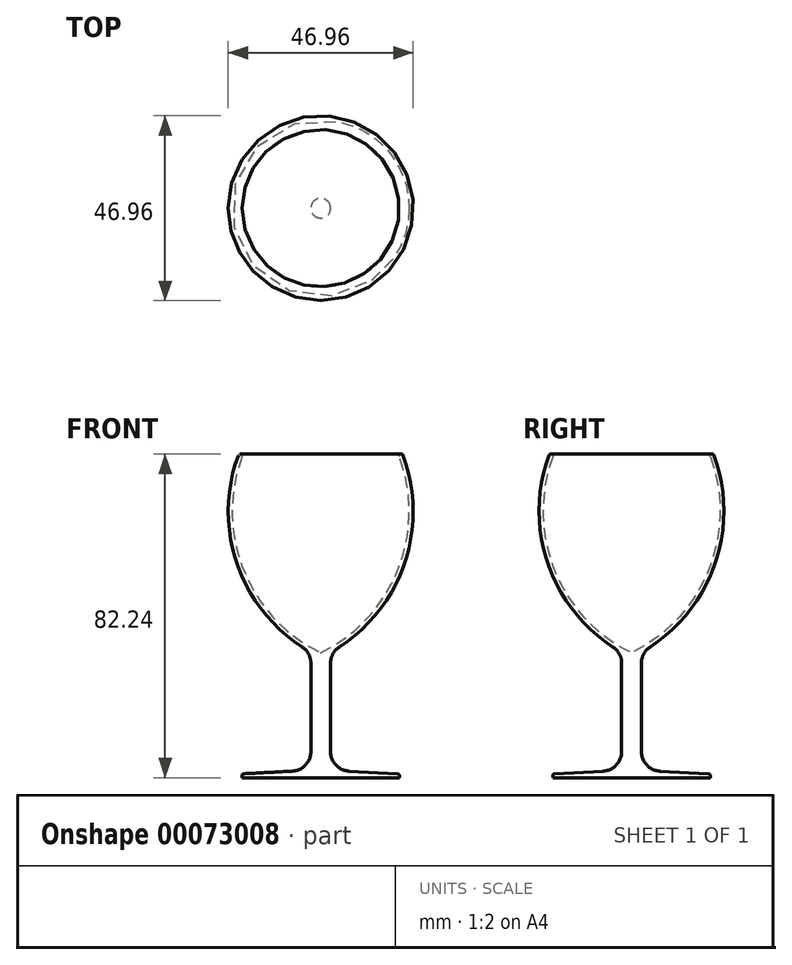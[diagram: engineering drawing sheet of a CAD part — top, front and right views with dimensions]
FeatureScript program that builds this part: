
annotation { "Feature Type Name" : "Feature", "Feature Type Description" : "" }
export const myFeature = defineFeature(function(context is Context, id is Id, definition is map)
    precondition{}
    {
        {
            var Q0;
            Q0=qCreatedBy(makeId("Front.planeOp"),FACE);
            var sketch = newSketch(context, id + "F0", { "sketchPlane" : qUnion([Q0])});
            skLineSegment(sketch, "E0", {"start": v(0, 0) * mm, "end": v(20, 0) * mm});
            skLineSegment(sketch, "E1", {"start": v(20, 0) * mm, "end": v(20, 1) * mm});
            skLineSegment(sketch, "E2", {"start": v(20, 1) * mm, "end": v(7.24, 1.67) * mm});
            skLineSegment(sketch, "E3", {"start": v(2.5, 6.66) * mm, "end": v(2.5, 29.1) * mm});
            skArc(sketch, "E4", {"start": v(4.78, 33.3) * mm, "mid": v(21.4, 54.77) * mm, "end": v(20.94, 81.92) * mm});
            skArc(sketch, "E5.0", {"start": v(0, 31.74) * mm, "mid": v(19.6, 52.8) * mm, "end": v(20, 81.57) * mm});
            skArc(sketch, "E6", {"start": v(20.94, 81.92) * mm, "mid": v(20.3, 82.21) * mm, "end": v(20, 81.57) * mm});
            skLineSegment(sketch, "E7", {"start": v(0, 0) * mm, "end": v(0, 31.74) * mm});
            skPoint(sketch, "E8.visualSharp", {"position": v(2.5, 31.92) * mm});
            skArc(sketch, "E8.filletArc", {"start": v(4.78, 33.3) * mm, "mid": v(3.1, 31.48) * mm, "end": v(2.5, 29.1) * mm});
            skPoint(sketch, "E9.visualSharp", {"position": v(2.5, 1.92) * mm});
            skArc(sketch, "E9.filletArc", {"start": v(2.5, 6.66) * mm, "mid": v(3.87, 3.22) * mm, "end": v(7.24, 1.67) * mm});
            skSolve(sketch);
        }
        {
            var Q0;
            Q0=makeQuery(id+"F0.imprint","IMPRINT",FACE,{"disambiguationData":[TD([[makeQuery(id+"F0.imprint","IMPRINT",EDGE,{"derivedFrom":sQuery(id+"F0.wireOp",EDGE,"E0")}),1.0]])]});
            var Q1;
            Q1=sQuery(id+"F0.wireOp",EDGE,"E7");
            revolve(context, id + "F1", {"entities" : qUnion([Q0]), "axis" : qUnion([Q1]), "revolveType" : RevolveType.FULL});
        }
        {
            var Q0;
            Q0=makeQuery(id+"F1.opRevolve","SWEPT_EDGE",EDGE,{"disambiguationData":[OSD([sQuery(id+"F0.wireOp",EDGE,"E1"),sQuery(id+"F0.wireOp",EDGE,"E2")])]});
            fillet(context, id + "F2", {"entities" : qUnion([Q0]), "radius" : .5 * mm, "tangentPropagation" : true, "allowEdgeOverflow" : false});
        }
    });
